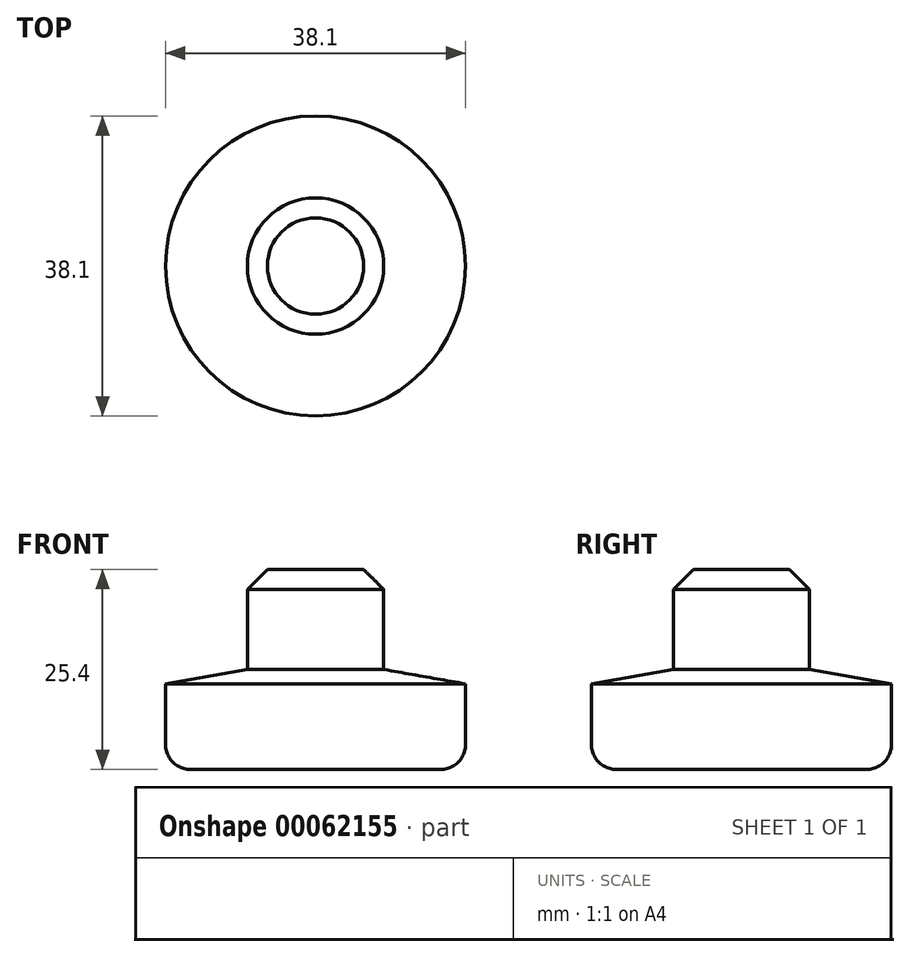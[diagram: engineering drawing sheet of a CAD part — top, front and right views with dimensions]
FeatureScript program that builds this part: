
annotation { "Feature Type Name" : "Feature", "Feature Type Description" : "" }
export const myFeature = defineFeature(function(context is Context, id is Id, definition is map)
    precondition{}
    {
        {
            var Q0;
            Q0=qCreatedBy(makeId("Top.planeOp"),FACE);
            var sketch = newSketch(context, id + "F0", { "sketchPlane" : qUnion([Q0])});
            skCircle(sketch, "E0", {"center": v(0, 0) * mm, "radius": 19.05 * mm});
            skSolve(sketch);
        }
        {
            var Q0;
            Q0=makeQuery(id+"F0.imprint","IMPRINT",FACE,{"disambiguationData":[TD([[makeQuery(id+"F0.imprint","IMPRINT",EDGE,{"derivedFrom":sQuery(id+"F0.wireOp",EDGE,"E0")}),1.0]])]});
            extrude(context, id + "F1", {"entities" : qUnion([Q0]), "oppositeDirection" : true, "depth" : 12.7 * mm});
        }
        {
            var Q0;
            Q0=makeQuery(id+"F1.opExtrude","CAP_FACE",FACE,{"disambiguationData":[OSD([sQuery(id+"F0.wireOp",EDGE,"E0")])],"isStart":true});
            var sketch = newSketch(context, id + "F2", { "sketchPlane" : qUnion([Q0])});
            skCircle(sketch, "E1", {"center": v(0, 0) * mm, "radius": 8.66 * mm});
            skSolve(sketch);
        }
        {
            var Q0;
            Q0=makeQuery(id+"F2.imprint","IMPRINT",FACE,{"disambiguationData":[TD([[makeQuery(id+"F2.imprint","IMPRINT",EDGE,{"derivedFrom":sQuery(id+"F2.wireOp",EDGE,"E1")}),1.0]])]});
            extrude(context, id + "F3", {"entities" : qUnion([Q0]), "operationType" : NewBodyOperationType.ADD, "depth" : 12.7 * mm});
        }
        {
            var Q0;
            Q0=makeQuery(id+"F3.opExtrude","CAP_EDGE",EDGE,{"disambiguationData":[OSD([sQuery(id+"F2.wireOp",EDGE,"E1")])],"isStart":false});
            chamfer(context, id + "F4", {"entities" : qUnion([Q0]), "width" : 2.54 * mm, "tangentPropagation" : true});
        }
        {
            var Q0;
            Q0=qCreatedBy(makeId("Front.planeOp"),FACE);
            var sketch = newSketch(context, id + "F5", { "sketchPlane" : qUnion([Q0])});
            skLineSegment(sketch, "E2", {"start": v(19.05, 0) * mm, "end": v(8.66, 0) * mm});
            skLineSegment(sketch, "E3", {"start": v(8.66, 0) * mm, "end": v(19.05, -1.83) * mm});
            skLineSegment(sketch, "E4", {"start": v(19.05, -1.83) * mm, "end": v(19.05, 0) * mm});
            skLineSegment(sketch, "E5", {"start": v(0, -2.06) * mm, "end": v(0, 10.98) * mm, "construction": true});
            skSolve(sketch);
        }
        {
            var Q0;
            Q0 = qSketchRegion(id + "F5", true);
            var Q1;
            Q1=sQuery(id+"F5.wireOp",EDGE,"E5");
            revolve(context, id + "F6", {"operationType" : NewBodyOperationType.REMOVE, "entities" : qUnion([Q0]), "axis" : qUnion([Q1]), "revolveType" : RevolveType.FULL, "oppositeDirection" : true});
        }
        {
            var Q0;
            Q0=makeQuery(id+"F1.opExtrude","CAP_EDGE",EDGE,{"disambiguationData":[OSD([sQuery(id+"F0.wireOp",EDGE,"E0")])],"isStart":false});
            fillet(context, id + "F7", {"entities" : qUnion([Q0]), "radius" : 3.17 * mm, "tangentPropagation" : true, "allowEdgeOverflow" : false});
        }
    });
